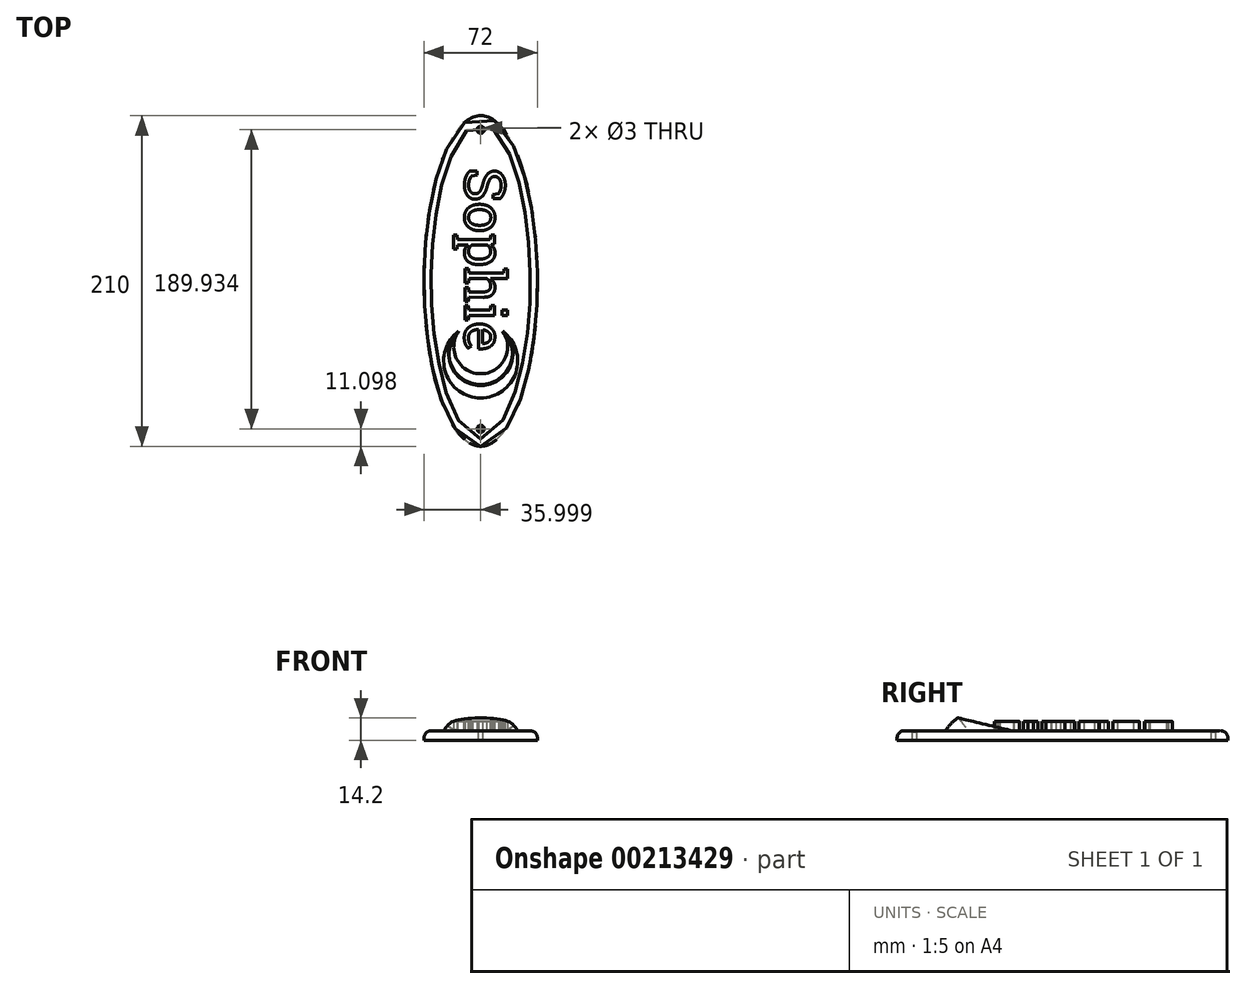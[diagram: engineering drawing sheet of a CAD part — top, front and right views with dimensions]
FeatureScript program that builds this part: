
annotation { "Feature Type Name" : "Feature", "Feature Type Description" : "" }
export const myFeature = defineFeature(function(context is Context, id is Id, definition is map)
    precondition{}
    {
        {
            var Q0;
            Q0=qCreatedBy(makeId("Top.planeOp"),FACE);
            var sketch = newSketch(context, id + "F0", { "sketchPlane" : qUnion([Q0])});
            skLineSegment(sketch, "E0", {"start": v(-4.66, 6.3) * mm, "end": v(0, 0) * mm, "construction": true});
            skLineSegment(sketch, "E1", {"start": v(0, 0) * mm, "end": v(4.66, 6.3) * mm, "construction": true});
            skArc(sketch, "E2", {"start": v(-4.66, 6.3) * mm, "mid": v(0, -7.84) * mm, "end": v(4.66, 6.3) * mm});
            skArc(sketch, "E3", {"start": v(-4.66, 6.3) * mm, "mid": v(0, -2.7) * mm, "end": v(4.66, 6.3) * mm});
            skSolve(sketch);
        }
        {
            var Q0;
            Q0=qCreatedBy(makeId("Front.planeOp"),FACE);
            var sketch = newSketch(context, id + "F1", { "sketchPlane" : qUnion([Q0])});
            skLineSegment(sketch, "E4", {"start": v(0, 0) * mm, "end": v(0, 1.5) * mm, "construction": true});
            skSolve(sketch);
        }
        {
            var Q0;
            Q0=sQuery(id+"F0.wireOp",VERTEX,"E0.start");
            var Q1;
            Q1=sQuery(id+"F0.wireOp",VERTEX,"E1.end");
            var Q2;
            Q2=sQuery(id+"F1.wireOp",VERTEX,"E4.end");
            cPlane(context, id + "F2", {"entities" : qUnion([Q0, Q1, Q2]), "cplaneType" : CPlaneType.THREE_POINT, "offset" : 150 * mm, "width" : 150 * mm, "height" : 150 * mm});
        }
        {
            var Q0;
            Q0=qCreatedBy(id+"F2.planeOp",FACE);
            var sketch = newSketch(context, id + "F3", { "sketchPlane" : qUnion([Q0])});
            skPoint(sketch, "E5.0", {"position": v(-4.66, 6.13) * mm});
            skPoint(sketch, "E6.0", {"position": v(4.66, 6.13) * mm});
            skPoint(sketch, "E7.0", {"position": v(0, 0) * mm});
            skLineSegment(sketch, "E8", {"start": v(0, 0) * mm, "end": v(0, -5.55) * mm, "construction": true});
            skPoint(sketch, "E9.third.point", {"position": v(0, -2.78) * mm});
            skArc(sketch, "E10", {"start": v(-4.66, 6.13) * mm, "mid": v(0, -5.45) * mm, "end": v(4.66, 6.13) * mm});
            skArc(sketch, "E11", {"start": v(-4.66, 6.13) * mm, "mid": v(0, -5.67) * mm, "end": v(4.66, 6.13) * mm});
            skSolve(sketch);
        }
        {
            var Q0;
            Q0=makeQuery(id+"F3.imprint","IMPRINT",FACE,{"disambiguationData":[TD([[makeQuery(id+"F3.imprint","IMPRINT",EDGE,{"derivedFrom":sQuery(id+"F3.wireOp",EDGE,"E10")}),-1.0]])]});
            var Q1;
            Q1=makeQuery(id+"F0.imprint","IMPRINT",FACE,{"disambiguationData":[TD([[makeQuery(id+"F0.imprint","IMPRINT",EDGE,{"derivedFrom":sQuery(id+"F0.wireOp",EDGE,"E2")}),1.0]])]});
            loft(context, id + "F4", {"sheetProfilesArray" : [{ "sheetProfileEntities" : qUnion([Q0]) }, { "sheetProfileEntities" : qUnion([Q1]) }]});
        }
        {
            var Q0;
            Q0=qCreatedBy(makeId("Top.planeOp"),FACE);
            var sketch = newSketch(context, id + "F5", { "sketchPlane" : qUnion([Q0])});
            skEllipse(sketch, "E12", {"center": v(0, 16.94) * mm, "majorRadius": 35 * mm, "minorRadius": 12 * mm, "majorAxis": v(0, -1)});
            skSolve(sketch);
        }
        {
            var Q0;
            Q0=makeQuery(id+"F5.imprint","IMPRINT",FACE,{"disambiguationData":[TD([[makeQuery(id+"F5.imprint","IMPRINT",EDGE,{"derivedFrom":sQuery(id+"F5.wireOp",EDGE,"E12")}),1.0]])]});
            extrude(context, id + "F6", {"entities" : qUnion([Q0]), "operationType" : NewBodyOperationType.ADD, "oppositeDirection" : true, "depth" : 2 * mm});
        }
        {
            var Q0;
            Q0=makeQuery(id+"F6.opExtrude","CAP_FACE",FACE,{"disambiguationData":[OSD([sQuery(id+"F5.wireOp",EDGE,"E12")])],"isStart":true});
            var sketch = newSketch(context, id + "F7", { "sketchPlane" : qUnion([Q0])});
            skText(sketch, "E13", { "text": "Sophie", "fontName": "RobotoSlab-Regular.ttf"});
            const initialGuessF7  = {"E13": [-0.00333, 0.04092, -0.00093, -1, 0.00853]};
            skSetInitialGuess(sketch, initialGuessF7);
            skSolve(sketch);
        }
        {
            var Q0;
            Q0 = qSketchRegion(id + "F7", true);
            extrude(context, id + "F8", {"entities" : qUnion([Q0]), "operationType" : NewBodyOperationType.ADD, "depth" : 2 * mm});
        }
        {
            var Q0;
            {var subQ0=sQuery(id+"F5.wireOp",EDGE,"E12");Q0=makeQuery(id+"F8.boolean.opBoolean","SPLIT",FACE,{"disambiguationData":[TD([makeQuery(id+"F6.opExtrude","SWEPT_FACE",FACE,{"disambiguationData":[OSD([subQ0])]})])],"derivedFrom":makeQuery(id+"F6.opExtrude","CAP_FACE",FACE,{"disambiguationData":[OSD([subQ0])],"isStart":true})});}
            var sketch = newSketch(context, id + "F9", { "sketchPlane" : qUnion([Q0])});
            skPoint(sketch, "E14", {"position": v(0, 48.95) * mm});
            skPoint(sketch, "E15", {"position": v(0, -14.36) * mm});
            skPoint(sketch, "E15.positionSnap0", {"position": v(0, -7.84) * mm});
            skSolve(sketch);
        }
        {
            var Q0;
            Q0=sQuery(id+"F9.wireOp",VERTEX,"E14");
            var Q1;
            Q1=sQuery(id+"F9.wireOp",VERTEX,"E15");
            var Q2;
            Q2=makeQuery(id+"F4.opLoft","SWEPT_BODY",BODY,{"disambiguationData":[OSD([makeQuery(id+"F0.imprint","IMPRINT",FACE,{"disambiguationData":[TD([[makeQuery(id+"F0.imprint","IMPRINT",EDGE,{"derivedFrom":sQuery(id+"F0.wireOp",EDGE,"E2")}),1.0]])]}),makeQuery(id+"F3.imprint","IMPRINT",FACE,{"disambiguationData":[TD([[makeQuery(id+"F3.imprint","IMPRINT",EDGE,{"derivedFrom":sQuery(id+"F3.wireOp",EDGE,"E10")}),-1.0]])]})])]});
            hole(context, id + "F10", {"style" : HoleStyle.C_SINK, "endStyle" : HoleEndStyle.BLIND, "holeDiameter" : 1 * mm, "cSinkDiameter" : 1.5 * mm, "cSinkAngle" : 90 * degree, "holeDepth" : 2 * mm, "locations" : qUnion([Q0, Q1]), "scope" : qUnion([Q2])});
        }
        {
            var Q0;
            Q0=makeQuery(id+"F6.opExtrude","CAP_EDGE",EDGE,{"disambiguationData":[OSD([sQuery(id+"F5.wireOp",EDGE,"E12")])],"isStart":true});
            fillet(context, id + "F11", {"entities" : qUnion([Q0]), "radius" : 1.5 * mm, "tangentPropagation" : true, "allowEdgeOverflow" : false});
        }
        {
            var Q0;
            Q0=makeQuery(id+"F4.opLoft","SWEPT_BODY",BODY,{"disambiguationData":[OSD([makeQuery(id+"F0.imprint","IMPRINT",FACE,{"disambiguationData":[TD([[makeQuery(id+"F0.imprint","IMPRINT",EDGE,{"derivedFrom":sQuery(id+"F0.wireOp",EDGE,"E2")}),1.0]])]}),makeQuery(id+"F3.imprint","IMPRINT",FACE,{"disambiguationData":[TD([[makeQuery(id+"F3.imprint","IMPRINT",EDGE,{"derivedFrom":sQuery(id+"F3.wireOp",EDGE,"E10")}),-1.0]])]})])]});
            var Q1;
            Q1=makeQuery(id+"F8.opExtrude","CAP_VERTEX",VERTEX,{"disambiguationData":[OSD([sQuery(id+"F7.wireOp",EDGE,"E13.sketch_text.stroke-100"),sQuery(id+"F7.wireOp",EDGE,"E13.sketch_text.stroke-101")])],"isStart":false});
            transform(context, id + "F12", {"entities" : qUnion([Q0]), "transformType" : TransformType.SCALE_UNIFORMLY, "scale" : 3, "scalePoint" : qUnion([Q1]), "makeCopy" : false});
        }
    });
